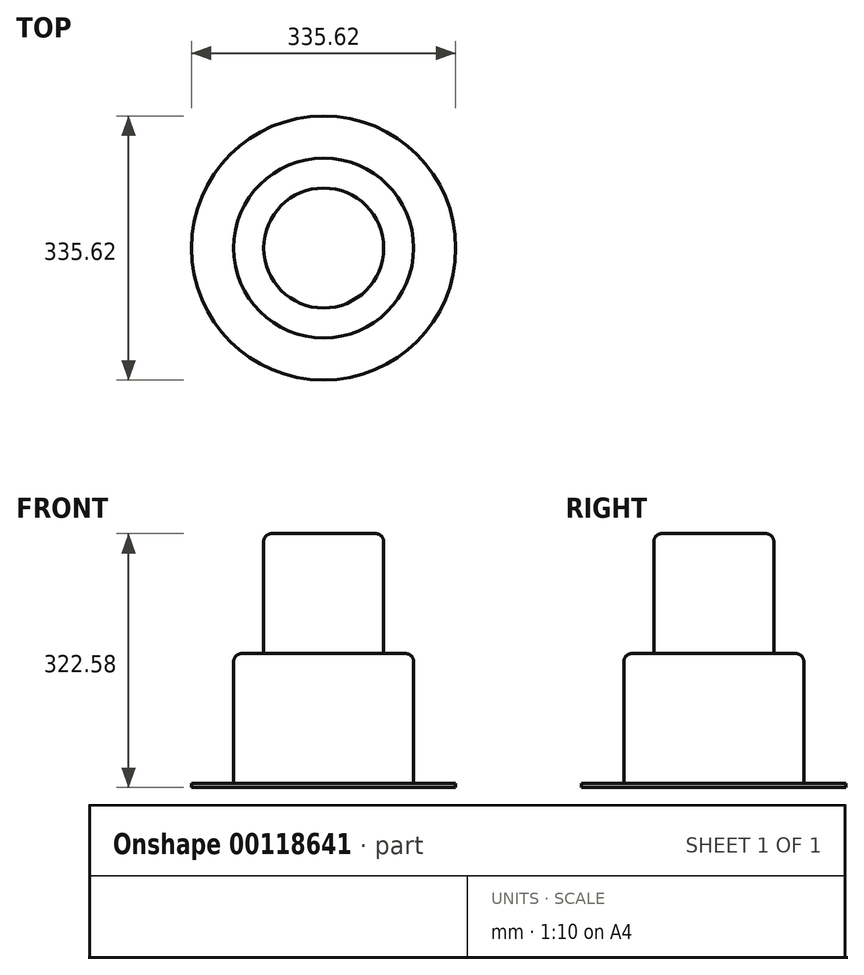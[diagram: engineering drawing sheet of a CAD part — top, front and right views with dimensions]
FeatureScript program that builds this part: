
annotation { "Feature Type Name" : "Feature", "Feature Type Description" : "" }
export const myFeature = defineFeature(function(context is Context, id is Id, definition is map)
    precondition{}
    {
        {
            var Q0;
            Q0=qCreatedBy(makeId("Top.planeOp"),FACE);
            var sketch = newSketch(context, id + "F0", { "sketchPlane" : qUnion([Q0])});
            skCircle(sketch, "E0", {"center": v(0, 0) * mm, "radius": 114.3 * mm});
            skSolve(sketch);
        }
        {
            var Q0;
            Q0 = qSketchRegion(id + "F0", true);
            extrude(context, id + "F1", {"entities" : qUnion([Q0]), "depth" : 165.1 * mm});
        }
        {
            var Q0;
            Q0=makeQuery(id+"F1.opExtrude","CAP_FACE",FACE,{"disambiguationData":[OSD([sQuery(id+"F0.wireOp",EDGE,"E0")])],"isStart":false});
            var sketch = newSketch(context, id + "F2", { "sketchPlane" : qUnion([Q0])});
            skCircle(sketch, "E1", {"center": v(0, 0) * mm, "radius": 76.2 * mm});
            skSolve(sketch);
        }
        {
            var Q0;
            Q0 = qSketchRegion(id + "F2", true);
            extrude(context, id + "F3", {"entities" : qUnion([Q0]), "operationType" : NewBodyOperationType.ADD, "depth" : 152.4 * mm});
        }
        {
            var Q0;
            Q0=makeQuery(id+"F1.opExtrude","CAP_EDGE",EDGE,{"disambiguationData":[OSD([sQuery(id+"F0.wireOp",EDGE,"E0")])],"isStart":false});
            var Q1;
            Q1=makeQuery(id+"F3.opExtrude","CAP_EDGE",EDGE,{"disambiguationData":[OSD([sQuery(id+"F2.wireOp",EDGE,"E1")])],"isStart":false});
            fillet(context, id + "F4", {"entities" : qUnion([Q0, Q1]), "radius" : 10.16 * mm, "tangentPropagation" : true, "allowEdgeOverflow" : false});
        }
        {
            var Q0;
            Q0=makeQuery(id+"F1.opExtrude","CAP_FACE",FACE,{"disambiguationData":[OSD([sQuery(id+"F0.wireOp",EDGE,"E0")])],"isStart":true});
            var sketch = newSketch(context, id + "F5", { "sketchPlane" : qUnion([Q0])});
            skCircle(sketch, "E2", {"center": v(0, 0) * mm, "radius": 167.81 * mm});
            skSolve(sketch);
        }
        {
            var Q0;
            Q0 = qSketchRegion(id + "F5", true);
            extrude(context, id + "F6", {"entities" : qUnion([Q0]), "operationType" : NewBodyOperationType.ADD, "depth" : 5.08 * mm});
        }
    });
